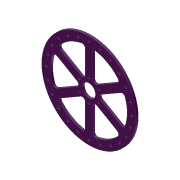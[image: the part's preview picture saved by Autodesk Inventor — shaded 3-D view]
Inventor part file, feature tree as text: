
AUTODESK INVENTOR PART (.ipt)
format: ipt  version: 2012 (Build 160160000, 160)  size: 174,592 bytes
history: native  units: in
note: dims shown in document units (in); Inventor stores cm internally (conversion verified against a paired STEP export)
features: extrude x4, sketch x4, pattern_circular x3
ambient origin geometry x8: Origin, YZ Plane, XZ Plane, XY Plane, X Axis, Y Axis, Z Axis, Center Point
bodies: Solid1 (feature_tree)
feature tree (11):
  extrude  "Extrusion1"  Depth=1.125in
  extrude  "Extrusion5"  Depth=0.375in
  pattern_circular  "Circular Pattern3"  Count=24 Angle=360.0deg
  extrude  "Extrusion6"  Depth=0.1875in
  pattern_circular  "Circular Pattern4"  [2 undecoded]
  extrude  "Extrusion7"  Depth=2.3622in TaperAngle=360.0deg
  pattern_circular  "Circular Pattern5"  [2 undecoded]
  sketch  "Sketch1"  dims[d0=8.0in d1=1.125in]
  sketch  "Sketch4"  dims[d27=0.1875in d28=0.0in d58=0.375in]
  sketch  "Sketch6"  dims[d59=0.1875in d60=0.0in d61=9.4488in d62=360.0deg]
  sketch  "Sketch7"  dims[d68=1.875in d69=0.1875in d70=0.1875in d71=0.0in d72=2.3622in d73=360.0deg d75=0.75in d76=0.25in d78=0.3125in d79=0.1875in d80=0.0in d81=2.3622in d82=360.0deg]
note: 4 required parameter values undecoded (feature->parameter linkage not recoverable at this tier; creation-order binding heuristic only, values carry confidence <= 0.55)
